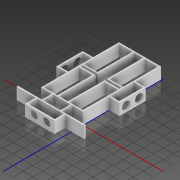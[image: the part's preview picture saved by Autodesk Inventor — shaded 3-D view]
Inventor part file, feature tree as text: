
AUTODESK INVENTOR PART (.ipt)
format: ipt  version: 2020.2 (Build 242310000, 310)  size: 325,632 bytes
history: native  units: mm
features: extrude x11, sketch x10
ambient origin geometry x8: Origin, YZ Plane, XZ Plane, XY Plane, X Axis, Y Axis, Z Axis, Center Point
bodies: Solid1 (feature_tree)
feature tree (21):
  sketch  "Sketch1"  dims[d1=156.0mm d12=3.0mm]
  extrude  "Extrusion1"  Depth=3.0mm
  sketch  "Sketch5"  dims[d13=3.0mm d15=70.0mm]
  extrude  "Extrusion6"  Depth=70.0mm
  sketch  "Sketch6"  dims[d17=70.0mm d18=23.0mm d19=0.0mm]
  extrude  "Extrusion7"  Depth=23.0mm TaperAngle=0.0deg
  extrude  "Extrusion10"  Depth=3.0mm
  extrude  "Extrusion9"  Depth=21.0mm TaperAngle=0.0deg
  extrude  "Extrusion11"  Depth=35.0mm
  extrude  "Extrusion12"  Depth=3.0mm
  extrude  "Extrusion13"  Depth=3.0mm
  extrude  "Extrusion14"  Depth=16.0mm
  extrude  "Extrusion15"  Depth=18.0mm
  extrude  "Extrusion16"  TaperAngle=180.0deg  [1 undecoded]
  sketch  "Sketch7"  dims[d66=3.0mm d68=3.0mm]
  sketch  "Sketch9"  dims[d80=21.0mm d81=0.0mm d92=24.25mm d93=0.0mm]
  sketch  "Sketch10"  dims[d97=35.0mm d98=35.0mm]
  sketch  "Sketch11"  dims[d99=3.0mm d100=3.0mm]
  sketch  "Sketch12"  dims[d101=3.0mm d102=3.0mm]
  sketch  "Sketch13"  dims[d108=16.0mm d109=16.0mm]
  sketch  "Sketch14"  dims[d110=10.0mm d111=0.0mm d112=18.0mm d113=180.0deg d114=3.0mm d115=21.0mm d116=23.5mm d117=0.0mm d118=13.4mm d119=11.5mm d120=13.4mm d121=11.5mm d122=16.0mm d123=13.4mm d124=11.5mm d125=16.0mm d126=10.0mm d127=0.0mm d128=25.0mm d129=3.0mm d130=25.0mm d131=3.0mm d132=23.0mm d133=0.0mm d134=3.0mm d135=47.5mm d136=87.5mm d137=0.0mm d138=0.0mm d139=38.1mm d140=3.0mm d141=38.1mm d142=3.0mm d143=21.0mm d144=0.0mm d145=3.0mm d146=60.25mm d147=0.0mm d148=16.8mm d149=11.5mm d150=16.0mm d151=16.8mm d152=11.5mm d153=16.0mm d154=10.0mm d155=0.0mm]
note: 1 required parameter value undecoded (feature->parameter linkage not recoverable at this tier; creation-order binding heuristic only, values carry confidence <= 0.55)
